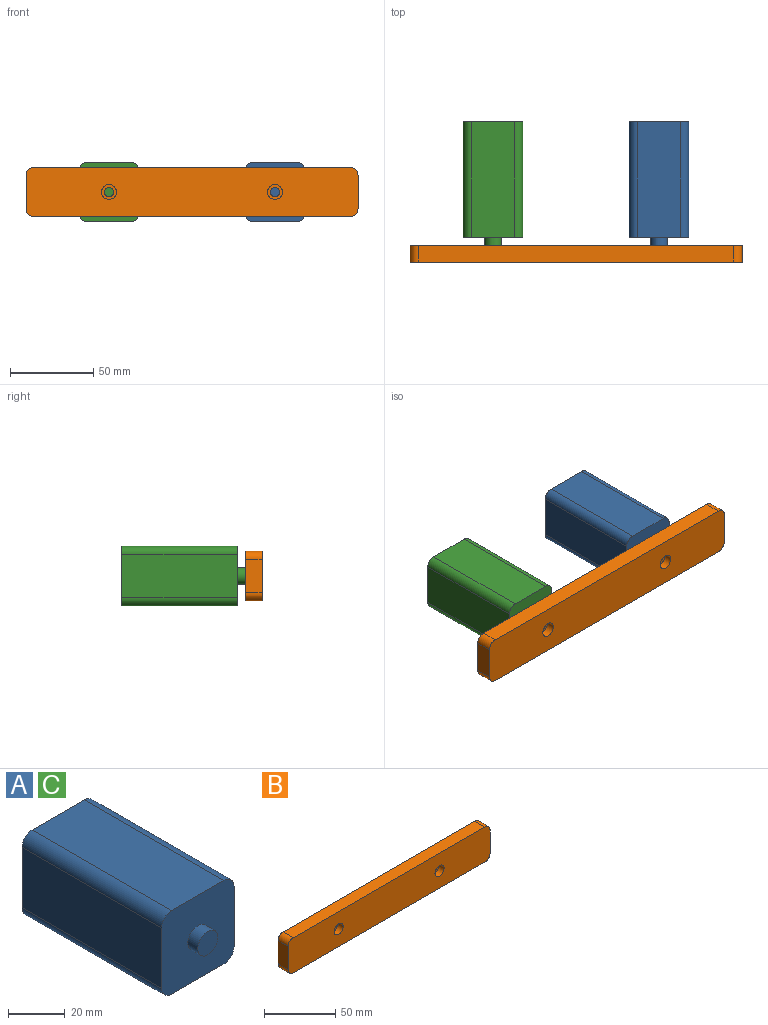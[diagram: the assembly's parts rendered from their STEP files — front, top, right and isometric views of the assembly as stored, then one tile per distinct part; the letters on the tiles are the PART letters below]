
ASSEMBLY  parts=3 mates=3
PART A: 12 faces, bbox 36x74.5x36 mm
  f0: plane 69.5x26mm, normal (1,0,0), area 1807mm2, adj f4,f5,f6,f9
  f1: plane 69.5x26mm, normal (0,0,1), area 1807mm2, adj f4,f5,f6,f7
  f2: plane 69.5x26mm, normal (-1,0,0), area 1807mm2, adj f4,f5,f7,f8
  f3: plane 69.5x26mm, normal (0,0,-1), area 1807mm2, adj f4,f5,f8,f9
  f4: plane 36x36mm, normal (0,-1,0), area 1196mm2, adj f0,f1,f2,f3,f6,f7,f8,f9
  f5: plane 36x36mm, normal (0,1,0), area 1274.5mm2, adj f0,f1,f2,f3,f6,f7,f8,f9
  f6: cylinder r=5mm len=69.5mm, axis (0,-1,0), area 545.9mm2, adj f0,f1,f4,f5
  f7: cylinder r=5mm len=69.5mm, axis (0,1,0), area 545.9mm2, adj f1,f2,f4,f5
  f8: cylinder r=5mm len=69.5mm, axis (0,-1,0), area 545.9mm2, adj f2,f3,f4,f5
  f9: cylinder r=5mm len=69.5mm, axis (0,1,0), area 545.9mm2, adj f0,f3,f4,f5
  f10: cylinder r=5mm len=10mm, axis (0,1,0), area 157.1mm2, adj f4,f11
  f11: plane 10x10mm, normal (0,-1,0), area 78.5mm2, adj f10
PART B: 16 faces, bbox 200x10x30 mm
  f0: cylinder r=2.75mm len=5.5mm, axis (0,1,0), area 86.4mm2, adj f7,f9
  f1: cylinder r=2.75mm len=5.5mm, axis (0,1,0), area 86.4mm2, adj f7,f11
  f2: plane 190x10mm, normal (0,0,1), area 1900mm2, adj f6,f7,f12,f15
  f3: plane 20x10mm, normal (-1,0,0), area 200mm2, adj f6,f7,f12,f13
  f4: plane 190x10mm, normal (0,0,-1), area 1900mm2, adj f6,f7,f13,f14
  f5: plane 20x10mm, normal (1,0,0), area 200mm2, adj f6,f7,f14,f15
  f6: plane 200x30mm, normal (0,-1,0), area 5851.3mm2, adj f2,f3,f4,f5,f8,f10,f12,f13
  f7: plane 200x30mm, normal (0,1,0), area 5931mm2, adj f0,f1,f2,f3,f4,f5,f12,f13
  f8: cylinder r=4.5mm len=9mm, axis (0,-1,0), area 141.4mm2, adj f6,f9
  f9: plane 9x9mm, normal (0,-1,0), area 39.9mm2, adj f0,f8
  f10: cylinder r=4.5mm len=9mm, axis (0,-1,0), area 141.4mm2, adj f6,f11
  f11: plane 9x9mm, normal (0,-1,0), area 39.9mm2, adj f1,f10
  f12: cylinder r=5mm len=10mm, axis (0,-1,0), area 78.5mm2, adj f2,f3,f6,f7
  f13: cylinder r=5mm len=10mm, axis (0,1,0), area 78.5mm2, adj f3,f4,f6,f7
  f14: cylinder r=5mm len=10mm, axis (0,-1,0), area 78.5mm2, adj f4,f5,f6,f7
  f15: cylinder r=5mm len=10mm, axis (0,1,0), area 78.5mm2, adj f2,f5,f6,f7
PART C: same geometry as A
PLACE A t=(5.2,34.05,11.95)mm
PLACE B t=(-94.8,34.05,11.95)mm
PLACE C t=(-94.8,34.05,11.95)mm
MATE fastened C.f10 <-> B.f1  axis (0,-1,0) through (-94.8,-5.7,11.95)mm
MATE planar C.f1 <-> A.f1  axis (0,0,1) through (-94.8,34.05,29.95)mm
MATE fastened A.f10 <-> B.f0  axis (0,-1,0) through (5.2,-5.7,11.95)mm
